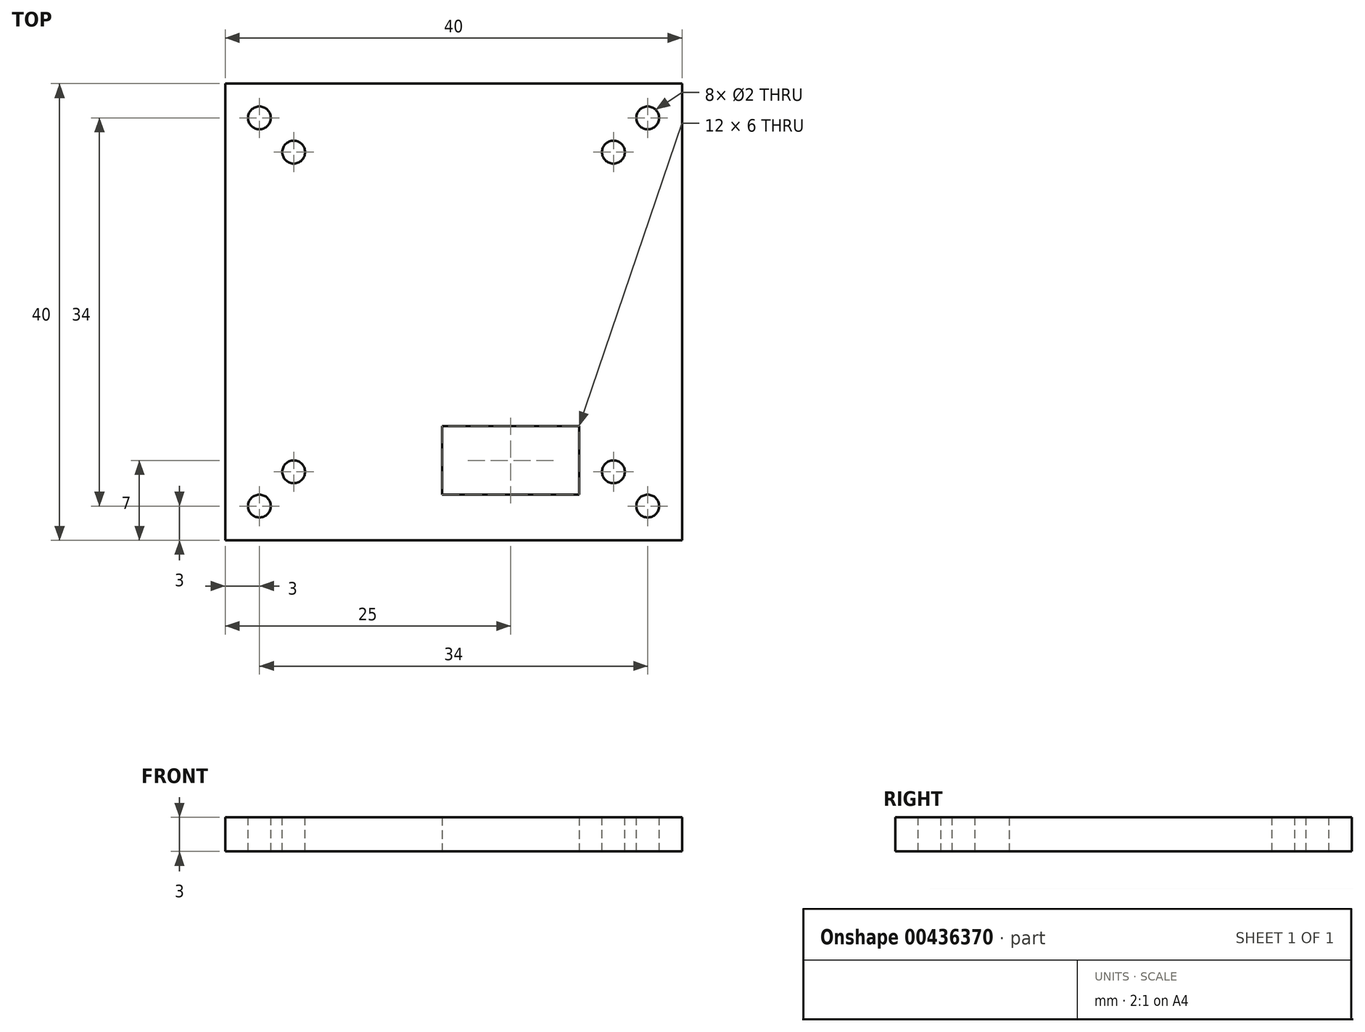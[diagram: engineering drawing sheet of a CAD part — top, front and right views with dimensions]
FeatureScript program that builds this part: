
annotation { "Feature Type Name" : "Feature", "Feature Type Description" : "" }
export const myFeature = defineFeature(function(context is Context, id is Id, definition is map)
    precondition{}
    {
        {
            var Q0;
            Q0=qCreatedBy(makeId("Top.planeOp"),FACE);
            var sketch = newSketch(context, id + "F0", { "sketchPlane" : qUnion([Q0])});
            skLineSegment(sketch, "E0.bottom", {"start": v(-20, 20) * mm, "end": v(20, 20) * mm});
            skLineSegment(sketch, "E0.top", {"start": v(-20, -20) * mm, "end": v(20, -20) * mm});
            skLineSegment(sketch, "E0.left", {"start": v(-20, 20) * mm, "end": v(-20, -20) * mm});
            skLineSegment(sketch, "E0.right", {"start": v(20, 20) * mm, "end": v(20, -20) * mm});
            skSolve(sketch);
        }
        {
            var Q0;
            Q0=qSketchRegion(id+"F0",true);
            extrude(context, id + "F1", {"entities" : qUnion([Q0]), "oppositeDirection" : true, "depth" : 3 * mm});
        }
        {
            var Q0;
            Q0=makeQuery(id+"F1.opExtrude","CAP_FACE",FACE,{"disambiguationData":[OSD([sQuery(id+"F0.wireOp",EDGE,"E0.bottom"),sQuery(id+"F0.wireOp",EDGE,"E0.top"),sQuery(id+"F0.wireOp",EDGE,"E0.left"),sQuery(id+"F0.wireOp",EDGE,"E0.right")])],"isStart":false});
            var sketch = newSketch(context, id + "F2", { "sketchPlane" : qUnion([Q0])});
            skLineSegment(sketch, "E1.bottom", {"start": v(11, 10) * mm, "end": v(-1, 10) * mm});
            skLineSegment(sketch, "E1.top", {"start": v(11, 16) * mm, "end": v(-1, 16) * mm});
            skLineSegment(sketch, "E1.left", {"start": v(11, 10) * mm, "end": v(11, 16) * mm});
            skLineSegment(sketch, "E1.right", {"start": v(-1, 10) * mm, "end": v(-1, 16) * mm});
            skSolve(sketch);
        }
        {
            var Q0;
            Q0=qSketchRegion(id+"F2",true);
            extrude(context, id + "F3", {"entities" : qUnion([Q0]), "operationType" : NewBodyOperationType.REMOVE, "oppositeDirection" : true, "depth" : 3 * mm});
        }
        {
            var Q0;
            Q0=makeQuery(id+"F1.opExtrude","CAP_FACE",FACE,{"disambiguationData":[OSD([sQuery(id+"F0.wireOp",EDGE,"E0.bottom"),sQuery(id+"F0.wireOp",EDGE,"E0.top"),sQuery(id+"F0.wireOp",EDGE,"E0.left"),sQuery(id+"F0.wireOp",EDGE,"E0.right")])],"isStart":true});
            var sketch = newSketch(context, id + "F4", { "sketchPlane" : qUnion([Q0])});
            skArc(sketch, "E2.0", {"start": v(-16, 17) * mm, "mid": v(-17.7, 17.7) * mm, "end": v(-17, 16) * mm});
            skCircle(sketch, "E3.0", {"center": v(-14, 14) * mm, "radius": 1 * mm});
            skCircle(sketch, "E4.0", {"center": v(14, 14) * mm, "radius": 1 * mm});
            skArc(sketch, "E5.0", {"start": v(17, 16) * mm, "mid": v(17.7, 17.7) * mm, "end": v(16, 17) * mm});
            skArc(sketch, "E6.0", {"start": v(-17, -16) * mm, "mid": v(-17.7, -17.7) * mm, "end": v(-16, -17) * mm});
            skCircle(sketch, "E7.0", {"center": v(-14, -14) * mm, "radius": 1 * mm});
            skCircle(sketch, "E8.0", {"center": v(14, -14) * mm, "radius": 1 * mm});
            skArc(sketch, "E9.0", {"start": v(16, -17) * mm, "mid": v(17.7, -17.7) * mm, "end": v(17, -16) * mm});
            skSolve(sketch);
        }
        {
            var Q0;
            Q0=sQuery(id+"F4.wireOp",VERTEX,"E2.0.center");
            var Q1;
            Q1=sQuery(id+"F4.wireOp",VERTEX,"E5.0.center");
            var Q2;
            Q2=sQuery(id+"F4.wireOp",VERTEX,"E4.0.center");
            var Q3;
            Q3=sQuery(id+"F4.wireOp",VERTEX,"E3.0.center");
            var Q4;
            Q4=sQuery(id+"F4.wireOp",VERTEX,"E6.0.center");
            var Q5;
            Q5=sQuery(id+"F4.wireOp",VERTEX,"E7.0.center");
            var Q6;
            Q6=sQuery(id+"F4.wireOp",VERTEX,"E8.0.center");
            var Q7;
            Q7=sQuery(id+"F4.wireOp",VERTEX,"E9.0.center");
            var Q8;
            Q8=makeQuery(id+"F1.opExtrude","SWEPT_BODY",BODY,{"disambiguationData":[OSD([sQuery(id+"F0.wireOp",EDGE,"E0.bottom"),sQuery(id+"F0.wireOp",EDGE,"E0.top"),sQuery(id+"F0.wireOp",EDGE,"E0.left"),sQuery(id+"F0.wireOp",EDGE,"E0.right")])]});
            hole(context, id + "F5", {"style" : HoleStyle.SIMPLE, "endStyle" : HoleEndStyle.BLIND, "holeDiameter" : 2 * mm, "holeDepth" : 10 * mm, "isTappedThrough" : true, "tappedDepth" : 12 * mm, "tapClearance" : 3, "startFromSketch" : true, "locations" : qUnion([Q0, Q1, Q2, Q3, Q4, Q5, Q6, Q7]), "scope" : qUnion([Q8])});
        }
    });
